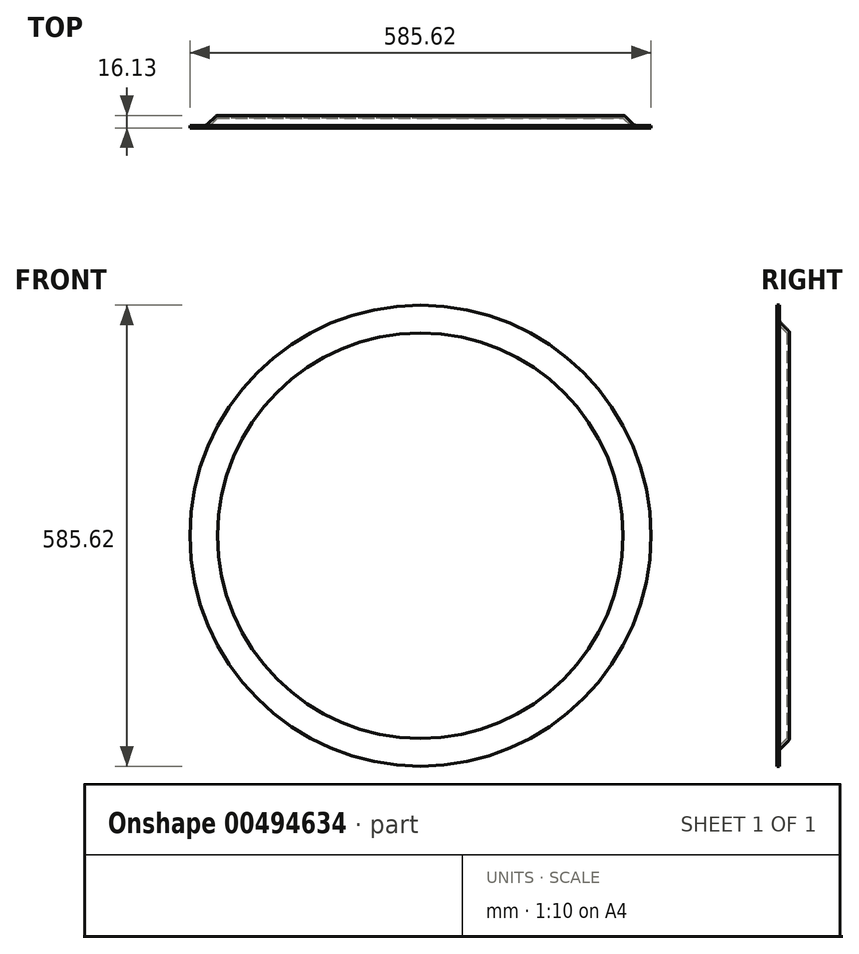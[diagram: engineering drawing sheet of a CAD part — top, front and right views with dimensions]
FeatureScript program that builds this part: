
annotation { "Feature Type Name" : "Feature", "Feature Type Description" : "" }
export const myFeature = defineFeature(function(context is Context, id is Id, definition is map)
    precondition{}
    {
        {
            var Q0;
            Q0=qCreatedBy(makeId("Top.planeOp"),FACE);
            var sketch = newSketch(context, id + "F0", { "sketchPlane" : qUnion([Q0])});
            skLineSegment(sketch, "E0", {"start": v(0, 0) * mm, "end": v(256.92, 0) * mm});
            skLineSegment(sketch, "E1", {"start": v(260.46, -1.46) * mm, "end": v(270.23, -11.24) * mm});
            skLineSegment(sketch, "E2", {"start": v(273.76, -12.7) * mm, "end": v(292.81, -12.7) * mm});
            skPoint(sketch, "E3.visualSharp", {"position": v(259, 0) * mm});
            skArc(sketch, "E3.filletArc", {"start": v(260.46, -1.46) * mm, "mid": v(258.83, -0.38) * mm, "end": v(256.92, 0) * mm});
            skPoint(sketch, "E4.visualSharp", {"position": v(271.7, -12.7) * mm});
            skArc(sketch, "E4.filletArc", {"start": v(270.23, -11.24) * mm, "mid": v(271.85, -12.32) * mm, "end": v(273.76, -12.7) * mm});
            skLineSegment(sketch, "E5.0", {"start": v(273.76, -16.13) * mm, "end": v(292.81, -16.13) * mm});
            skArc(sketch, "E5.1", {"start": v(267.8, -13.66) * mm, "mid": v(270.54, -15.49) * mm, "end": v(273.76, -16.13) * mm});
            skLineSegment(sketch, "E5.2", {"start": v(257.57, -3.43) * mm, "end": v(267.8, -13.66) * mm});
            skLineSegment(sketch, "E5.3", {"start": v(0, -3.43) * mm, "end": v(257.57, -3.43) * mm});
            skLineSegment(sketch, "E6", {"start": v(0, 0) * mm, "end": v(0, -3.43) * mm});
            skLineSegment(sketch, "E7", {"start": v(292.81, -12.7) * mm, "end": v(292.81, -16.13) * mm});
            skSolve(sketch);
        }
        {
            var Q0;
            Q0=makeQuery(id+"F0.imprint","IMPRINT",FACE,{"disambiguationData":[TD([[makeQuery(id+"F0.imprint","IMPRINT",EDGE,{"derivedFrom":sQuery(id+"F0.wireOp",EDGE,"E0")}),-1.0]])]});
            var Q1;
            Q1=sQuery(id+"F0.wireOp",EDGE,"E6");
            revolve(context, id + "F1", {"entities" : qUnion([Q0]), "axis" : qUnion([Q1]), "revolveType" : RevolveType.FULL});
        }
    });
